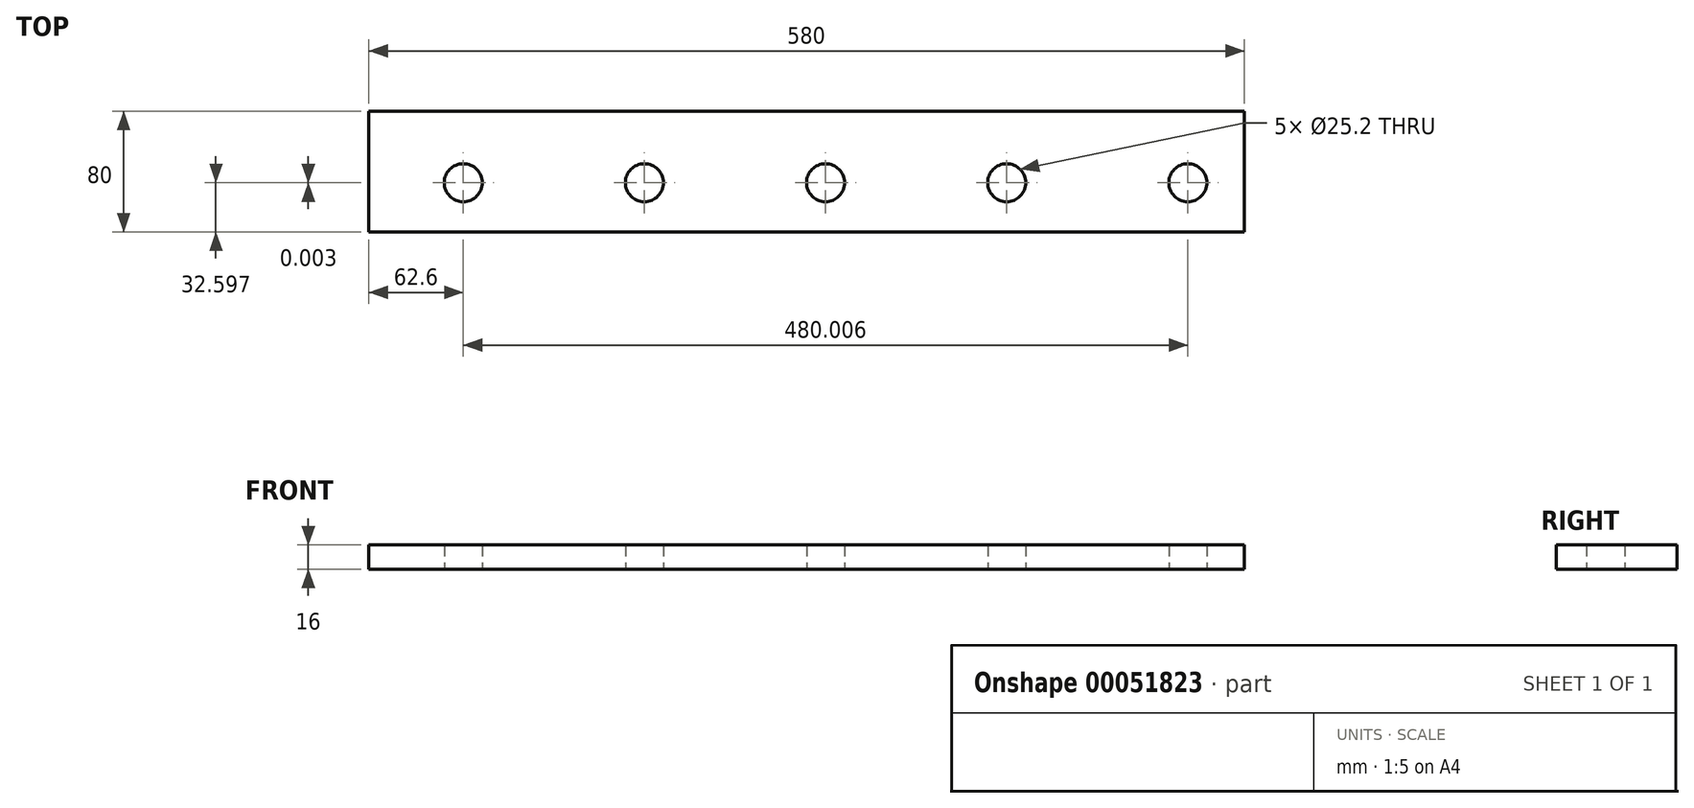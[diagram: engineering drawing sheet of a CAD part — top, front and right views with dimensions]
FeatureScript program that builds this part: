
annotation { "Feature Type Name" : "Feature", "Feature Type Description" : "" }
export const myFeature = defineFeature(function(context is Context, id is Id, definition is map)
    precondition{}
    {
        {
            var Q0;
            Q0=qCreatedBy(makeId("Top.planeOp"),FACE);
            var sketch = newSketch(context, id + "F0", { "sketchPlane" : qUnion([Q0])});
            skLineSegment(sketch, "E0.rect.bottom", {"start": v(-290, 40) * mm, "end": v(290, 40) * mm});
            skLineSegment(sketch, "E0.rect.top", {"start": v(-290, -40) * mm, "end": v(290, -40) * mm});
            skLineSegment(sketch, "E0.rect.left", {"start": v(-290, 40) * mm, "end": v(-290, -40) * mm});
            skLineSegment(sketch, "E0.rect.right", {"start": v(290, 40) * mm, "end": v(290, -40) * mm});
            skPoint(sketch, "E0.rect.middle", {"position": v(0, 0) * mm});
            skCircle(sketch, "E1", {"center": v(-227.4, -7.4) * mm, "radius": 12.6 * mm});
            skCircle(sketch, "E2", {"center": v(-107.4, -7.4) * mm, "radius": 12.6 * mm});
            skCircle(sketch, "E3", {"center": v(12.6, -7.4) * mm, "radius": 12.6 * mm});
            skCircle(sketch, "E4", {"center": v(252.6, -7.4) * mm, "radius": 12.6 * mm});
            skCircle(sketch, "E5", {"center": v(132.6, -7.4) * mm, "radius": 12.6 * mm});
            skLineSegment(sketch, "E6", {"start": v(-227.4, -7.4) * mm, "end": v(-107.4, -7.4) * mm, "construction": true});
            skLineSegment(sketch, "E7", {"start": v(-107.4, -7.4) * mm, "end": v(12.6, -7.4) * mm, "construction": true});
            skLineSegment(sketch, "E8", {"start": v(12.6, -7.4) * mm, "end": v(132.6, -7.4) * mm, "construction": true});
            skLineSegment(sketch, "E9", {"start": v(132.6, -7.4) * mm, "end": v(252.6, -7.4) * mm, "construction": true});
            skSolve(sketch);
        }
        {
            var Q0;
            Q0=makeQuery(id+"F0.imprint","IMPRINT",FACE,{"disambiguationData":[TD([[makeQuery(id+"F0.imprint","IMPRINT",EDGE,{"derivedFrom":sQuery(id+"F0.wireOp",EDGE,"E0.rect.bottom")}),-1.0]])]});
            extrude(context, id + "F1", {"entities" : qUnion([Q0]), "depth" : 16 * mm});
        }
    });
